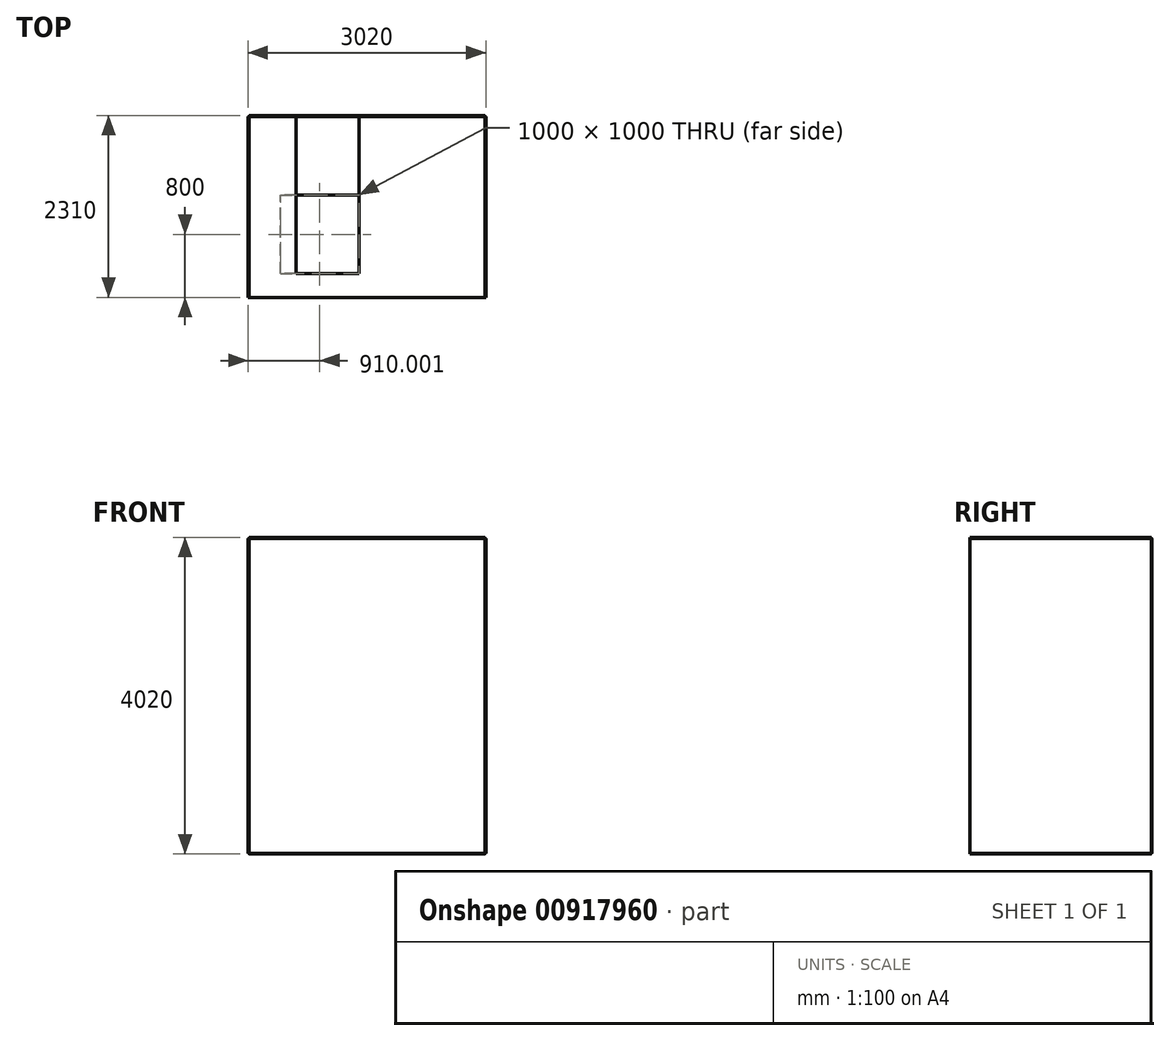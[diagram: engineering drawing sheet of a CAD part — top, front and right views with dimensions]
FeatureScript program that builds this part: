
annotation { "Feature Type Name" : "Feature", "Feature Type Description" : "" }
export const myFeature = defineFeature(function(context is Context, id is Id, definition is map)
    precondition{}
    {
        {
            var Q0;
            Q0=qCreatedBy(makeId("Front.planeOp"),FACE);
            var sketch = newSketch(context, id + "F0", { "sketchPlane" : qUnion([Q0])});
            skLineSegment(sketch, "E0.bottom", {"start": v(-112.68, 3940.49) * mm, "end": v(2887.32, 3940.49) * mm});
            skLineSegment(sketch, "E0.top", {"start": v(-112.68, -59.51) * mm, "end": v(2887.32, -59.51) * mm});
            skLineSegment(sketch, "E0.left", {"start": v(-112.68, 3940.49) * mm, "end": v(-112.68, -59.51) * mm});
            skLineSegment(sketch, "E0.right", {"start": v(2887.32, 3940.49) * mm, "end": v(2887.32, -59.51) * mm});
            skSolve(sketch);
        }
        {
            var Q0;
            Q0 = qSketchRegion(id + "F0", true);
            extrude(context, id + "F1", {"entities" : qUnion([Q0]), "depth" : 10 * mm, "offsetDistance" : 25 * mm});
        }
        {
            var Q0;
            Q0=makeQuery(id+"F1.opExtrude","CAP_FACE",FACE,{"disambiguationData":[OSD([sQuery(id+"F0.wireOp",EDGE,"E0.bottom"),sQuery(id+"F0.wireOp",EDGE,"E0.top"),sQuery(id+"F0.wireOp",EDGE,"E0.left"),sQuery(id+"F0.wireOp",EDGE,"E0.right")])],"isStart":false});
            var sketch = newSketch(context, id + "F2", { "sketchPlane" : qUnion([Q0])});
            skLineSegment(sketch, "E1.bottom", {"start": v(-112.68, 3940.49) * mm, "end": v(-122.68, 3940.49) * mm});
            skLineSegment(sketch, "E1.top", {"start": v(-112.68, -59.51) * mm, "end": v(-122.68, -59.51) * mm});
            skLineSegment(sketch, "E1.left", {"start": v(-112.68, 3940.49) * mm, "end": v(-112.68, -59.51) * mm});
            skLineSegment(sketch, "E1.right", {"start": v(-122.68, 3940.49) * mm, "end": v(-122.68, -59.51) * mm});
            skSolve(sketch);
        }
        {
            var Q0;
            Q0 = qSketchRegion(id + "F2", true);
            extrude(context, id + "F3", {"entities" : qUnion([Q0]), "depth" : 2300 * mm, "offsetDistance" : 25 * mm});
        }
        {
            var Q0;
            Q0=makeQuery(id+"F1.opExtrude","CAP_FACE",FACE,{"disambiguationData":[OSD([sQuery(id+"F0.wireOp",EDGE,"E0.bottom"),sQuery(id+"F0.wireOp",EDGE,"E0.top"),sQuery(id+"F0.wireOp",EDGE,"E0.left"),sQuery(id+"F0.wireOp",EDGE,"E0.right")])],"isStart":false});
            var sketch = newSketch(context, id + "F4", { "sketchPlane" : qUnion([Q0])});
            skLineSegment(sketch, "E2.bottom", {"start": v(2887.32, 3940.49) * mm, "end": v(-112.68, 3940.49) * mm});
            skLineSegment(sketch, "E2.top", {"start": v(2887.32, 3950.49) * mm, "end": v(-112.68, 3950.49) * mm});
            skLineSegment(sketch, "E2.left", {"start": v(2887.32, 3940.49) * mm, "end": v(2887.32, 3950.49) * mm});
            skLineSegment(sketch, "E2.right", {"start": v(-112.68, 3940.49) * mm, "end": v(-112.68, 3950.49) * mm});
            skSolve(sketch);
        }
        {
            var Q0;
            Q0 = qSketchRegion(id + "F4", true);
            extrude(context, id + "F5", {"entities" : qUnion([Q0]), "depth" : 2300 * mm, "offsetDistance" : 25 * mm});
        }
        {
            var Q0;
            Q0=makeQuery(id+"F1.opExtrude","CAP_FACE",FACE,{"disambiguationData":[OSD([sQuery(id+"F0.wireOp",EDGE,"E0.bottom"),sQuery(id+"F0.wireOp",EDGE,"E0.top"),sQuery(id+"F0.wireOp",EDGE,"E0.left"),sQuery(id+"F0.wireOp",EDGE,"E0.right")])],"isStart":false});
            var sketch = newSketch(context, id + "F6", { "sketchPlane" : qUnion([Q0])});
            skLineSegment(sketch, "E3.bottom", {"start": v(2887.32, 3940.49) * mm, "end": v(2897.32, 3940.49) * mm});
            skLineSegment(sketch, "E3.top", {"start": v(2887.32, -59.51) * mm, "end": v(2897.32, -59.51) * mm});
            skLineSegment(sketch, "E3.left", {"start": v(2887.32, 3940.49) * mm, "end": v(2887.32, -59.51) * mm});
            skLineSegment(sketch, "E3.right", {"start": v(2897.32, 3940.49) * mm, "end": v(2897.32, -59.51) * mm});
            skSolve(sketch);
        }
        {
            var Q0;
            Q0=makeQuery(id+"F6.imprint","IMPRINT",FACE,{"disambiguationData":[TD([[makeQuery(id+"F6.imprint","IMPRINT",EDGE,{"derivedFrom":sQuery(id+"F6.wireOp",EDGE,"E3.bottom")}),-1.0]])]});
            extrude(context, id + "F7", {"entities" : qUnion([Q0]), "depth" : 2300 * mm, "offsetDistance" : 25 * mm});
        }
        {
            var Q0;
            Q0=makeQuery(id+"F1.opExtrude","CAP_FACE",FACE,{"disambiguationData":[OSD([sQuery(id+"F0.wireOp",EDGE,"E0.bottom"),sQuery(id+"F0.wireOp",EDGE,"E0.top"),sQuery(id+"F0.wireOp",EDGE,"E0.left"),sQuery(id+"F0.wireOp",EDGE,"E0.right")])],"isStart":false});
            var sketch = newSketch(context, id + "F8", { "sketchPlane" : qUnion([Q0])});
            skLineSegment(sketch, "E4.bottom", {"start": v(-112.68, -59.51) * mm, "end": v(2887.32, -59.51) * mm});
            skLineSegment(sketch, "E4.top", {"start": v(-112.68, -69.51) * mm, "end": v(2887.32, -69.51) * mm});
            skLineSegment(sketch, "E4.left", {"start": v(-112.68, -59.51) * mm, "end": v(-112.68, -69.51) * mm});
            skLineSegment(sketch, "E4.right", {"start": v(2887.32, -59.51) * mm, "end": v(2887.32, -69.51) * mm});
            skSolve(sketch);
        }
        {
            var Q0;
            Q0 = qSketchRegion(id + "F8", true);
            extrude(context, id + "F9", {"entities" : qUnion([Q0]), "depth" : 2300 * mm, "offsetDistance" : 25 * mm});
        }
        {
            var Q0;
            Q0=makeQuery(id+"F9.opExtrude","SWEPT_FACE",FACE,{"disambiguationData":[OSD([sQuery(id+"F8.wireOp",EDGE,"E4.bottom")])]});
            var sketch = newSketch(context, id + "F10", { "sketchPlane" : qUnion([Q0])});
            skLineSegment(sketch, "E5.bottom", {"start": v(1287.32, -2010) * mm, "end": v(287.32, -2010) * mm});
            skLineSegment(sketch, "E5.top", {"start": v(1287.32, -1010) * mm, "end": v(287.32, -1010) * mm});
            skLineSegment(sketch, "E5.left", {"start": v(1287.32, -2010) * mm, "end": v(1287.32, -1010) * mm});
            skLineSegment(sketch, "E5.right", {"start": v(287.32, -2010) * mm, "end": v(287.32, -1010) * mm});
            skSolve(sketch);
        }
        {
            var Q0;
            Q0=makeQuery(id+"F10.imprint","IMPRINT",FACE,{"disambiguationData":[TD([[makeQuery(id+"F10.imprint","IMPRINT",EDGE,{"derivedFrom":sQuery(id+"F10.wireOp",EDGE,"E5.bottom")}),-1.0]])]});
            extrude(context, id + "F11", {"entities" : qUnion([Q0]), "operationType" : NewBodyOperationType.REMOVE, "endBound" : BoundingType.UP_TO_NEXT, "oppositeDirection" : true, "depth" : 25 * mm, "offsetDistance" : 25 * mm});
        }
        {
            var Q0;
            Q0=makeQuery(id+"F5.opExtrude","SWEPT_FACE",FACE,{"disambiguationData":[OSD([sQuery(id+"F4.wireOp",EDGE,"E2.top")])]});
            var sketch = newSketch(context, id + "F12", { "sketchPlane" : qUnion([Q0])});
            skLineSegment(sketch, "E6.bottom", {"start": v(1287.32, -2010) * mm, "end": v(487.32, -2010) * mm});
            skLineSegment(sketch, "E6.top", {"start": v(1287.32, -10) * mm, "end": v(487.32, -10) * mm});
            skLineSegment(sketch, "E6.left", {"start": v(1287.32, -2010) * mm, "end": v(1287.32, -10) * mm});
            skLineSegment(sketch, "E6.right", {"start": v(487.32, -2010) * mm, "end": v(487.32, -10) * mm});
            skSolve(sketch);
        }
        {
            var Q0;
            Q0 = qSketchRegion(id + "F12", true);
            extrude(context, id + "F13", {"entities" : qUnion([Q0]), "operationType" : NewBodyOperationType.REMOVE, "endBound" : BoundingType.UP_TO_NEXT, "oppositeDirection" : true, "depth" : 25 * mm, "offsetDistance" : 25 * mm});
        }
    });
